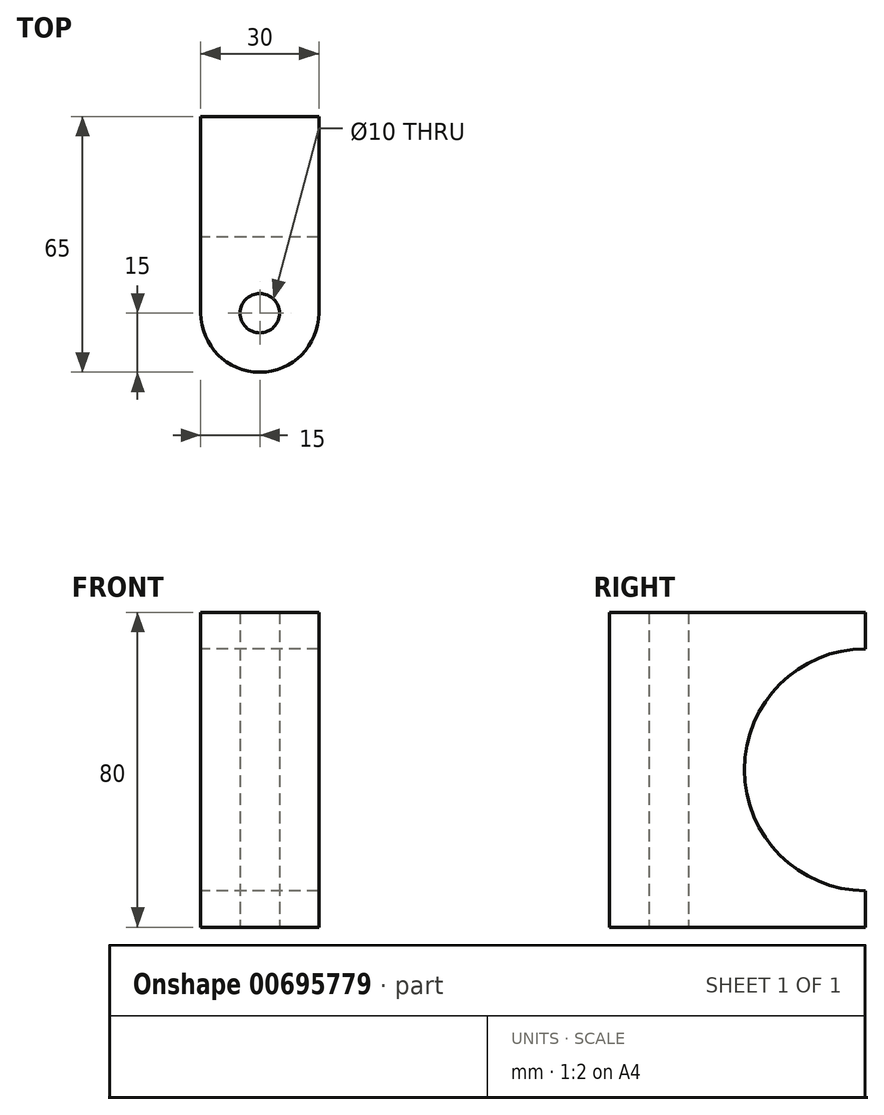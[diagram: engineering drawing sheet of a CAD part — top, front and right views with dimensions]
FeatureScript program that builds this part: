
annotation { "Feature Type Name" : "Feature", "Feature Type Description" : "" }
export const myFeature = defineFeature(function(context is Context, id is Id, definition is map)
    precondition{}
    {
        {
            var Q0;
            Q0=qCreatedBy(makeId("Top.planeOp"),FACE);
            var sketch = newSketch(context, id + "F0", { "sketchPlane" : qUnion([Q0])});
            skCircle(sketch, "E0", {"center": v(0, 0) * mm, "radius": 15 * mm});
            skLineSegment(sketch, "E1", {"start": v(-15, 50) * mm, "end": v(15, 50) * mm});
            skLineSegment(sketch, "E2", {"start": v(15, 50) * mm, "end": v(15, 0) * mm});
            skLineSegment(sketch, "E3", {"start": v(-15, 50) * mm, "end": v(-15, 0) * mm});
            skSolve(sketch);
        }
        {
            var Q0;
            Q0 = qSketchRegion(id + "F0", true);
            extrude(context, id + "F1", {"entities" : qUnion([Q0]), "depth" : 80 * mm, "offsetDistance" : 25 * mm});
        }
        {
            var Q0;
            Q0=makeQuery(id+"F1.opExtrude","SWEPT_FACE",FACE,{"disambiguationData":[OSD([sQuery(id+"F0.wireOp",EDGE,"E3")])]});
            var sketch = newSketch(context, id + "F2", { "sketchPlane" : qUnion([Q0])});
            skLineSegment(sketch, "E4.0", {"start": v(-50, 80) * mm, "end": v(-50, 70.73) * mm});
            skArc(sketch, "E5", {"start": v(-50, 9.27) * mm, "mid": v(-19.27, 40) * mm, "end": v(-50, 70.73) * mm});
            skLineSegment(sketch, "E6.trimOffspring", {"start": v(-50, 9.27) * mm, "end": v(-50, 0) * mm});
            skLineSegment(sketch, "E7", {"start": v(-50, 70.73) * mm, "end": v(-50, 9.27) * mm});
            skSolve(sketch);
        }
        {
            var Q0;
            Q0=makeQuery(id+"F2.imprint","IMPRINT",FACE,{"disambiguationData":[TD([[makeQuery(id+"F2.imprint","IMPRINT",EDGE,{"derivedFrom":sQuery(id+"F2.wireOp",EDGE,"E5")}),1.0]])]});
            extrude(context, id + "F3", {"entities" : qUnion([Q0]), "operationType" : NewBodyOperationType.REMOVE, "oppositeDirection" : true, "depth" : 55 * mm, "offsetDistance" : 25 * mm});
        }
        {
            var Q0;
            Q0=makeQuery(id+"F1.opExtrude","CAP_FACE",FACE,{"disambiguationData":[OSD([sQuery(id+"F0.wireOp",EDGE,"E0"),sQuery(id+"F0.wireOp",EDGE,"E1"),sQuery(id+"F0.wireOp",EDGE,"E2"),sQuery(id+"F0.wireOp",EDGE,"E3")])],"isStart":true});
            var sketch = newSketch(context, id + "F4", { "sketchPlane" : qUnion([Q0])});
            skPoint(sketch, "E8", {"position": v(0, 0) * mm});
            skSolve(sketch);
        }
        {
            var Q0;
            Q0=sQuery(id+"F4.wireOp",VERTEX,"E8");
            var Q1;
            Q1=makeQuery(id+"F1.opExtrude","SWEPT_BODY",BODY,{"disambiguationData":[OSD([sQuery(id+"F0.wireOp",EDGE,"E0"),sQuery(id+"F0.wireOp",EDGE,"E1"),sQuery(id+"F0.wireOp",EDGE,"E2"),sQuery(id+"F0.wireOp",EDGE,"E3")])]});
            hole(context, id + "F5", {"style" : HoleStyle.SIMPLE, "endStyle" : HoleEndStyle.THROUGH, "holeDiameter" : 10 * mm, "majorDiameter" : 5 * mm, "isTappedThrough" : true, "tappedDepth" : 12 * mm, "tapClearance" : 3, "locations" : qUnion([Q0]), "scope" : qUnion([Q1])});
        }
    });
